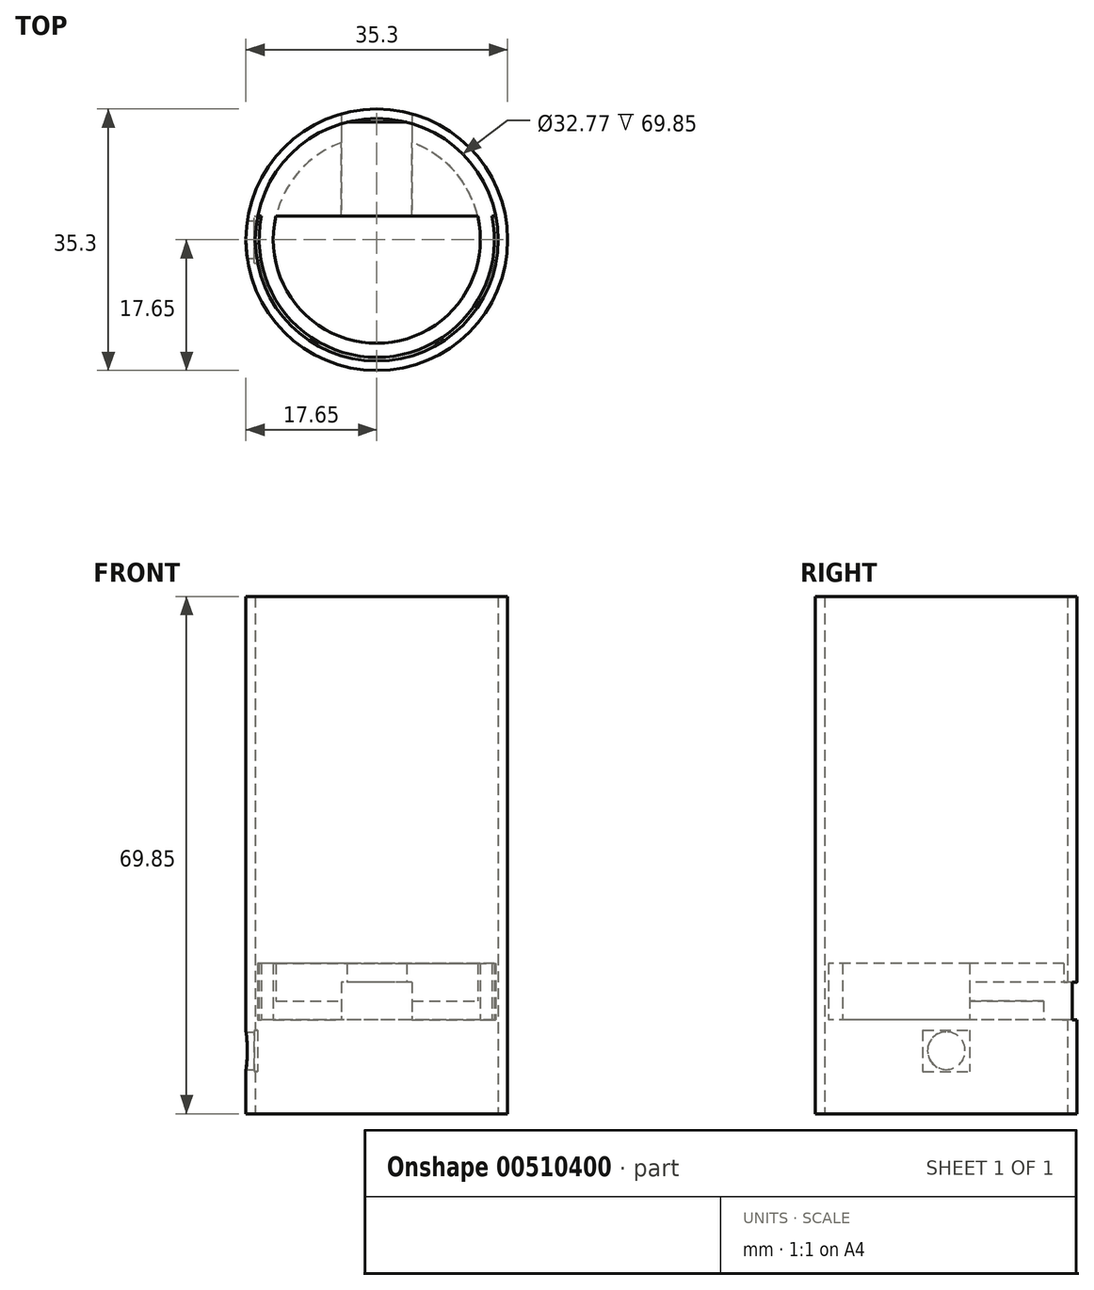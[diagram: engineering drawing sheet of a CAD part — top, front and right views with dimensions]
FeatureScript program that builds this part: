
annotation { "Feature Type Name" : "Feature", "Feature Type Description" : "" }
export const myFeature = defineFeature(function(context is Context, id is Id, definition is map)
    precondition{}
    {
        {
            var Q0;
            Q0=qCreatedBy(makeId("Top.planeOp"),FACE);
            var sketch = newSketch(context, id + "F0", { "sketchPlane" : qUnion([Q0])});
            skCircle(sketch, "E0", {"center": v(0, 0) * mm, "radius": 16.38 * mm});
            skCircle(sketch, "E1", {"center": v(0, 0) * mm, "radius": 17.65 * mm});
            skSolve(sketch);
        }
        {
            var Q0;
            Q0=makeQuery(id+"F0.imprint","IMPRINT",FACE,{"disambiguationData":[TD([[makeQuery(id+"F0.imprint","IMPRINT",EDGE,{"derivedFrom":sQuery(id+"F0.wireOp",EDGE,"E0")}),-1.0]])]});
            var Q1;
            Q1=sQuery(id+"F0.wireOp",EDGE,"E1");
            extrude(context, id + "F1", {"entities" : qUnion([Q0]), "surfaceEntities" : qUnion([Q1]), "depth" : 69.85 * mm});
        }
        {
            var Q0;
            Q0=qCreatedBy(makeId("Right.planeOp"),FACE);
            var sketch = newSketch(context, id + "F2", { "sketchPlane" : qUnion([Q0])});
            skLineSegment(sketch, "E2.bottom", {"start": v(15.87, 20.32) * mm, "end": v(3.17, 20.32) * mm});
            skLineSegment(sketch, "E2.top", {"start": v(15.87, 12.7) * mm, "end": v(3.17, 12.7) * mm});
            skLineSegment(sketch, "E2.left", {"start": v(15.87, 20.32) * mm, "end": v(15.87, 12.7) * mm});
            skLineSegment(sketch, "E2.right", {"start": v(3.17, 20.32) * mm, "end": v(3.17, 12.7) * mm});
            skSolve(sketch);
        }
        {
            var Q0;
            Q0=qCreatedBy(makeId("Front.planeOp"),FACE);
            var sketch = newSketch(context, id + "F3", { "sketchPlane" : qUnion([Q0])});
            skLineSegment(sketch, "E3.bottom", {"start": v(4.76, 17.78) * mm, "end": v(-4.76, 17.78) * mm});
            skLineSegment(sketch, "E3.top", {"start": v(4.76, 12.7) * mm, "end": v(-4.76, 12.7) * mm});
            skLineSegment(sketch, "E3.left", {"start": v(4.76, 17.78) * mm, "end": v(4.76, 12.7) * mm});
            skLineSegment(sketch, "E3.right", {"start": v(-4.76, 17.78) * mm, "end": v(-4.76, 12.7) * mm});
            skSolve(sketch);
        }
        {
            var Q0;
            Q0=qSketchRegion(id+"F2",true);
            extrude(context, id + "F4", {"entities" : qUnion([Q0]), "operationType" : NewBodyOperationType.ADD, "endBound" : BoundingType.UP_TO_NEXT, "oppositeDirection" : true, "depth" : 7.62 * mm});
        }
        {
            var Q0;
            Q0=makeQuery(id+"F2.imprint","IMPRINT",FACE,{"disambiguationData":[TD([[makeQuery(id+"F2.imprint","IMPRINT",EDGE,{"derivedFrom":sQuery(id+"F2.wireOp",EDGE,"E2.bottom")}),1.0]])]});
            extrude(context, id + "F5", {"entities" : qUnion([Q0]), "operationType" : NewBodyOperationType.ADD, "endBound" : BoundingType.UP_TO_NEXT, "depth" : 25.4 * mm});
        }
        {
            var Q0;
            Q0=qCreatedBy(makeId("Right.planeOp"),FACE);
            var sketch = newSketch(context, id + "F6", { "sketchPlane" : qUnion([Q0])});
            skCircle(sketch, "E4", {"center": v(0, 8.5) * mm, "radius": 2.54 * mm});
            skSolve(sketch);
        }
        {
            var Q0;
            Q0=qSketchRegion(id+"F6",true);
            extrude(context, id + "F7", {"entities" : qUnion([Q0]), "operationType" : NewBodyOperationType.REMOVE, "oppositeDirection" : true, "depth" : 25.4 * mm});
        }
        {
            var Q0;
            {var subQ1=sQuery(id+"F2.wireOp",EDGE,"E2.top");Q0=makeQuery(id+"F12.boolean.opBoolean","SPLIT",FACE,{"disambiguationData":[TD([makeQuery(id+"F12.opExtrude","SWEPT_FACE",FACE,{"disambiguationData":[OSD([sQuery(id+"F3.wireOp",EDGE,"E3.left")])]})])],"derivedFrom":makeQuery(id+"F5.boolean.opBoolean","MERGE",FACE,{"derivedFrom":[makeQuery(id+"F4.opExtrude","SWEPT_FACE",FACE,{"disambiguationData":[OSD([subQ1])]}),makeQuery(id+"F5.opExtrude","SWEPT_FACE",FACE,{"disambiguationData":[OSD([subQ1])]})]})});}
            var sketch = newSketch(context, id + "F8", { "sketchPlane" : qUnion([Q0])});
            skCircle(sketch, "E5", {"center": v(0, 0) * mm, "radius": 13.97 * mm});
            skCircle(sketch, "E6", {"center": v(0, 0) * mm, "radius": 15.88 * mm});
            skCircle(sketch, "E7", {"center": v(0, 0) * mm, "radius": 0.36 * mm});
            skSolve(sketch);
        }
        {
            var Q0;
            Q0=qSketchRegion(id+"F8",true);
            extrude(context, id + "F9", {"entities" : qUnion([Q0]), "operationType" : NewBodyOperationType.ADD, "oppositeDirection" : true, "depth" : 2.54 * mm});
        }
        {
            var Q0;
            Q0=qSketchRegion(id+"F8",true);
            var Q1;
            Q1=sQuery(id+"F8.wireOp",EDGE,"E5");
            extrude(context, id + "F10", {"entities" : qUnion([Q0]), "operationType" : NewBodyOperationType.ADD, "surfaceEntities" : qUnion([Q1]), "oppositeDirection" : true, "depth" : 7.62 * mm});
        }
        {
            var Q0;
            {var subQ0=sQuery(id+"F8.wireOp",EDGE,"E5");var subQ1=sQuery(id+"F2.wireOp",EDGE,"E2.right");var subQ2=sQuery(id+"F2.wireOp",EDGE,"E2.top");var subQ3=makeQuery(id+"F5.boolean.opBoolean","MERGE",EDGE,{"derivedFrom":[makeQuery(id+"F4.opExtrude","SWEPT_EDGE",EDGE,{"disambiguationData":[OSD([subQ2,subQ1])]}),makeQuery(id+"F5.opExtrude","SWEPT_EDGE",EDGE,{"disambiguationData":[OSD([subQ2,subQ1])]})]});var subQ4=makeQuery(id+"F8.imprint","INTERSECT",VERTEX,{"disambiguationData":[OD(0.0)],"derivedFrom":[subQ3,subQ0]});Q0=makeQuery(id+"F8.imprint","IMPRINT",FACE,{"disambiguationData":[TD([[makeQuery(id+"F8.imprint","IMPRINT",EDGE,{"disambiguationData":[TD([[subQ4,-1.0]])],"derivedFrom":subQ0}),1.0]])]});}
            extrude(context, id + "F11", {"entities" : qUnion([Q0]), "operationType" : NewBodyOperationType.REMOVE, "oppositeDirection" : true, "depth" : 2.54 * mm});
        }
        {
            var Q0;
            Q0=qSketchRegion(id+"F3",true);
            extrude(context, id + "F12", {"entities" : qUnion([Q0]), "operationType" : NewBodyOperationType.REMOVE, "oppositeDirection" : true, "depth" : 25.4 * mm});
        }
        {
            var Q0;
            Q0=qCreatedBy(makeId("Right.planeOp"),FACE);
            var sketch = newSketch(context, id + "F13", { "sketchPlane" : qUnion([Q0])});
            skLineSegment(sketch, "E8.bottom", {"start": v(-3.17, 11.3) * mm, "end": v(3.17, 11.3) * mm});
            skLineSegment(sketch, "E8.top", {"start": v(-3.17, 5.72) * mm, "end": v(3.18, 5.72) * mm});
            skLineSegment(sketch, "E8.left", {"start": v(-3.17, 11.3) * mm, "end": v(-3.17, 5.71) * mm});
            skLineSegment(sketch, "E8.right", {"start": v(3.17, 11.3) * mm, "end": v(3.18, 5.72) * mm});
            skSolve(sketch);
        }
        {
            var Q0;
            Q0=qSketchRegion(id+"F13",true);
            extrude(context, id + "F14", {"entities" : qUnion([Q0]), "operationType" : NewBodyOperationType.REMOVE, "oppositeDirection" : true, "depth" : 16.5 * mm});
        }
    });
